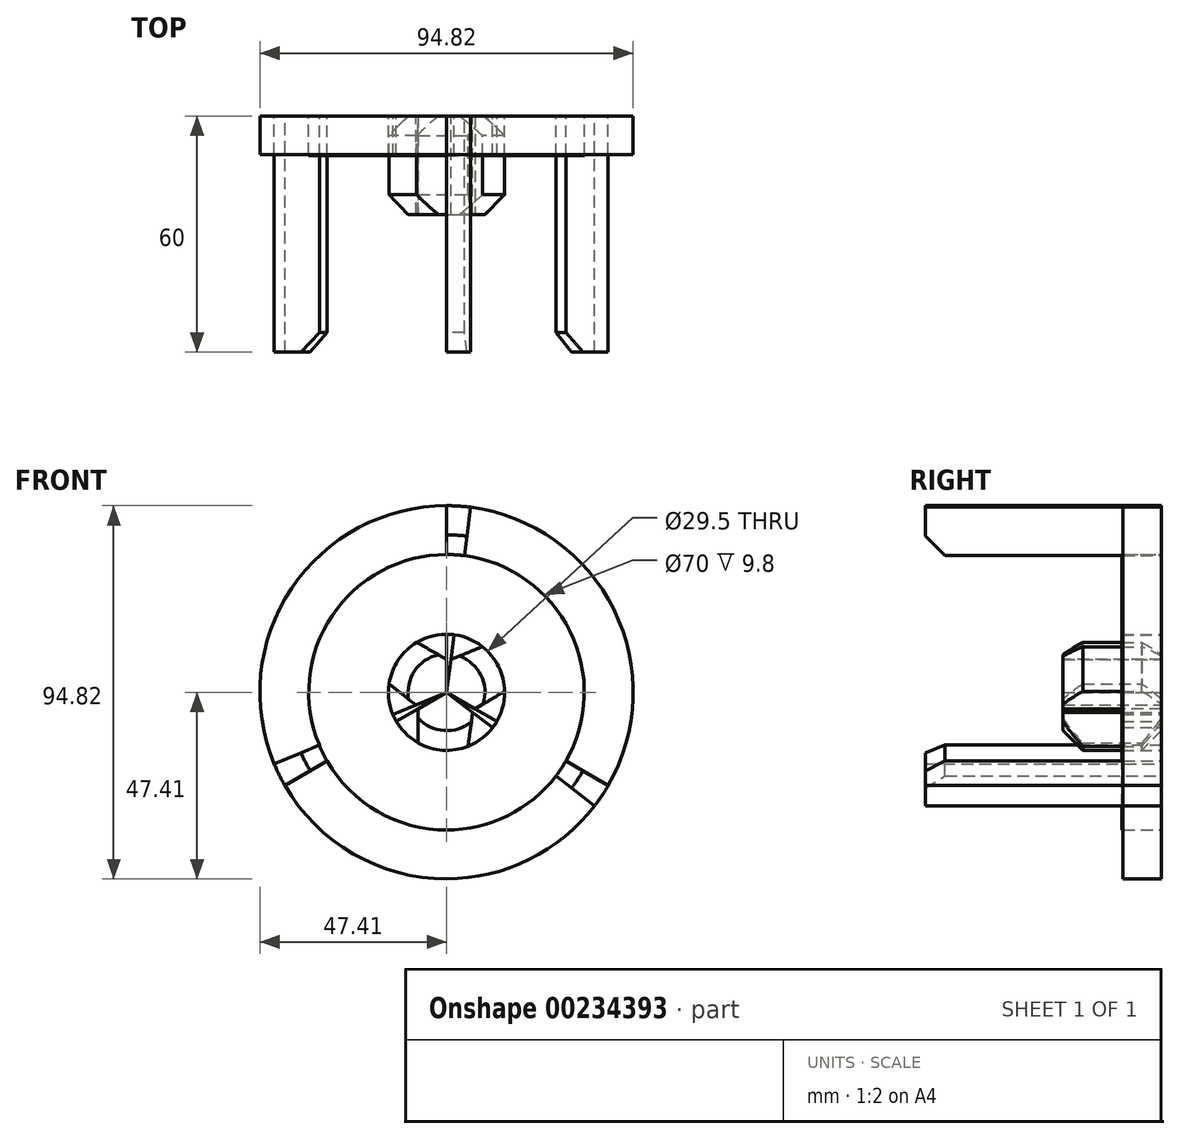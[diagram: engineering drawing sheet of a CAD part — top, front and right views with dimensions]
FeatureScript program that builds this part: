
annotation { "Feature Type Name" : "Feature", "Feature Type Description" : "" }
export const myFeature = defineFeature(function(context is Context, id is Id, definition is map)
    precondition{}
    {
        {
            var Q0;
            Q0=qCreatedBy(makeId("Front.planeOp"),FACE);
            var sketch = newSketch(context, id + "F0", { "sketchPlane" : qUnion([Q0])});
            skCircle(sketch, "E0", {"center": v(0, 0) * mm, "radius": 35 * mm});
            skCircle(sketch, "E1", {"center": v(0, 0) * mm, "radius": 47.41 * mm});
            skLineSegment(sketch, "E2", {"start": v(0, 0) * mm, "end": v(0, 47.41) * mm});
            skLineSegment(sketch, "E3.1.0", {"start": v(0, 0) * mm, "end": v(-41.06, -23.7) * mm});
            skLineSegment(sketch, "E3.2.0", {"start": v(0, 0) * mm, "end": v(41.06, -23.7) * mm});
            skLineSegment(sketch, "E4", {"start": v(0, 0) * mm, "end": v(6.14, 47.01) * mm});
            skLineSegment(sketch, "E5.1.0", {"start": v(0, 0) * mm, "end": v(-43.79, -18.2) * mm});
            skLineSegment(sketch, "E5.2.0", {"start": v(0, 0) * mm, "end": v(37.65, -28.82) * mm});
            skCircle(sketch, "E6", {"center": v(0, 0) * mm, "radius": 14.75 * mm});
            skSolve(sketch);
        }
        {
            var Q0;
            {var subQ0=sQuery(id+"F0.wireOp",EDGE,"E2");var subQ1=sQuery(id+"F0.wireOp",EDGE,"E0");var subQ2=makeQuery(id+"F0.imprint","INTERSECT",VERTEX,{"derivedFrom":[subQ1,subQ0]});Q0=makeQuery(id+"F0.imprint","IMPRINT",FACE,{"disambiguationData":[TD([[makeQuery(id+"F0.imprint","IMPRINT",EDGE,{"disambiguationData":[TD([[subQ2,1.0]])],"derivedFrom":subQ1}),-1.0]])]});}
            var Q1;
            {var subQ0=sQuery(id+"F0.wireOp",EDGE,"E5.2.0");var subQ1=sQuery(id+"F0.wireOp",EDGE,"E0");var subQ2=makeQuery(id+"F0.imprint","INTERSECT",VERTEX,{"derivedFrom":[subQ1,subQ0]});Q1=makeQuery(id+"F0.imprint","IMPRINT",FACE,{"disambiguationData":[TD([[makeQuery(id+"F0.imprint","IMPRINT",EDGE,{"disambiguationData":[TD([[subQ2,-1.0]])],"derivedFrom":subQ1}),-1.0]])]});}
            var Q2;
            {var subQ0=sQuery(id+"F0.wireOp",EDGE,"E5.1.0");var subQ1=sQuery(id+"F0.wireOp",EDGE,"E0");var subQ2=makeQuery(id+"F0.imprint","INTERSECT",VERTEX,{"derivedFrom":[subQ1,subQ0]});Q2=makeQuery(id+"F0.imprint","IMPRINT",FACE,{"disambiguationData":[TD([[makeQuery(id+"F0.imprint","IMPRINT",EDGE,{"disambiguationData":[TD([[subQ2,-1.0]])],"derivedFrom":subQ1}),-1.0]])]});}
            extrude(context, id + "F1", {"entities" : qUnion([Q0, Q1, Q2]), "depth" : 60 * mm});
        }
        {
            var Q0;
            Q0 = qSketchRegion(id + "F0", true);
            extrude(context, id + "F2", {"entities" : qUnion([Q0]), "depth" : 9.8 * mm});
        }
        {
            var Q0;
            {var subQ1=sQuery(id+"F0.wireOp",EDGE,"E2");var subQ3=sQuery(id+"F0.wireOp",EDGE,"E6");var subQ4=makeQuery(id+"F0.imprint","INTERSECT",VERTEX,{"derivedFrom":[subQ1,subQ3]});Q0=makeQuery(id+"F0.imprint","IMPRINT",FACE,{"disambiguationData":[TD([[makeQuery(id+"F0.imprint","IMPRINT",EDGE,{"disambiguationData":[TD([[subQ4,-1.0]])],"derivedFrom":subQ3}),1.0]])]});}
            var Q1;
            {var subQ1=sQuery(id+"F0.wireOp",EDGE,"E3.2.0");var subQ3=sQuery(id+"F0.wireOp",EDGE,"E6");var subQ4=makeQuery(id+"F0.imprint","INTERSECT",VERTEX,{"derivedFrom":[subQ1,subQ3]});Q1=makeQuery(id+"F0.imprint","IMPRINT",FACE,{"disambiguationData":[TD([[makeQuery(id+"F0.imprint","IMPRINT",EDGE,{"disambiguationData":[TD([[subQ4,-1.0]])],"derivedFrom":subQ3}),1.0]])]});}
            var Q2;
            {var subQ1=sQuery(id+"F0.wireOp",EDGE,"E3.1.0");var subQ3=sQuery(id+"F0.wireOp",EDGE,"E6");var subQ4=makeQuery(id+"F0.imprint","INTERSECT",VERTEX,{"derivedFrom":[subQ1,subQ3]});Q2=makeQuery(id+"F0.imprint","IMPRINT",FACE,{"disambiguationData":[TD([[makeQuery(id+"F0.imprint","IMPRINT",EDGE,{"disambiguationData":[TD([[subQ4,-1.0]])],"derivedFrom":subQ3}),1.0]])]});}
            extrude(context, id + "F3", {"entities" : qUnion([Q0, Q1, Q2]), "depth" : 25 * mm});
        }
        {
            var Q0;
            {var subQ0=sQuery(id+"F0.wireOp",EDGE,"E3.1.0");var subQ1=sQuery(id+"F0.wireOp",EDGE,"E0");var subQ2=makeQuery(id+"F0.imprint","INTERSECT",VERTEX,{"derivedFrom":[subQ1,subQ0]});Q0=makeQuery(id+"F0.imprint","IMPRINT",FACE,{"disambiguationData":[TD([[makeQuery(id+"F0.imprint","IMPRINT",EDGE,{"disambiguationData":[TD([[subQ2,-1.0]])],"derivedFrom":subQ1}),1.0]])]});}
            var Q1;
            {var subQ0=sQuery(id+"F0.wireOp",EDGE,"E4");var subQ1=sQuery(id+"F0.wireOp",EDGE,"E0");var subQ2=makeQuery(id+"F0.imprint","INTERSECT",VERTEX,{"derivedFrom":[subQ1,subQ0]});Q1=makeQuery(id+"F0.imprint","IMPRINT",FACE,{"disambiguationData":[TD([[makeQuery(id+"F0.imprint","IMPRINT",EDGE,{"disambiguationData":[TD([[subQ2,1.0]])],"derivedFrom":subQ1}),1.0]])]});}
            var Q2;
            {var subQ0=sQuery(id+"F0.wireOp",EDGE,"E5.2.0");var subQ1=sQuery(id+"F0.wireOp",EDGE,"E0");var subQ2=makeQuery(id+"F0.imprint","INTERSECT",VERTEX,{"derivedFrom":[subQ1,subQ0]});Q2=makeQuery(id+"F0.imprint","IMPRINT",FACE,{"disambiguationData":[TD([[makeQuery(id+"F0.imprint","IMPRINT",EDGE,{"disambiguationData":[TD([[subQ2,-1.0]])],"derivedFrom":subQ1}),1.0]])]});}
            var Q3;
            {var subQ0=sQuery(id+"F0.wireOp",EDGE,"E5.1.0");var subQ1=sQuery(id+"F0.wireOp",EDGE,"E0");var subQ2=makeQuery(id+"F0.imprint","INTERSECT",VERTEX,{"derivedFrom":[subQ1,subQ0]});Q3=makeQuery(id+"F0.imprint","IMPRINT",FACE,{"disambiguationData":[TD([[makeQuery(id+"F0.imprint","IMPRINT",EDGE,{"disambiguationData":[TD([[subQ2,-1.0]])],"derivedFrom":subQ1}),1.0]])]});}
            var Q4;
            {var subQ0=sQuery(id+"F0.wireOp",EDGE,"E2");var subQ1=sQuery(id+"F0.wireOp",EDGE,"E0");var subQ2=makeQuery(id+"F0.imprint","INTERSECT",VERTEX,{"derivedFrom":[subQ1,subQ0]});Q4=makeQuery(id+"F0.imprint","IMPRINT",FACE,{"disambiguationData":[TD([[makeQuery(id+"F0.imprint","IMPRINT",EDGE,{"disambiguationData":[TD([[subQ2,-1.0]])],"derivedFrom":subQ1}),1.0]])]});}
            var Q5;
            {var subQ0=sQuery(id+"F0.wireOp",EDGE,"E2");var subQ1=sQuery(id+"F0.wireOp",EDGE,"E0");var subQ2=makeQuery(id+"F0.imprint","INTERSECT",VERTEX,{"derivedFrom":[subQ1,subQ0]});Q5=makeQuery(id+"F0.imprint","IMPRINT",FACE,{"disambiguationData":[TD([[makeQuery(id+"F0.imprint","IMPRINT",EDGE,{"disambiguationData":[TD([[subQ2,1.0]])],"derivedFrom":subQ1}),1.0]])]});}
            extrude(context, id + "F4", {"entities" : qUnion([Q0, Q1, Q2, Q3, Q4, Q5]), "depth" : 10 * mm});
        }
        {
            var Q0;
            {var subQ1=sQuery(id+"F0.wireOp",EDGE,"E3.2.0");var subQ3=sQuery(id+"F0.wireOp",EDGE,"E6");var subQ4=makeQuery(id+"F0.imprint","INTERSECT",VERTEX,{"derivedFrom":[subQ1,subQ3]});Q0=makeQuery(id+"F0.imprint","IMPRINT",FACE,{"disambiguationData":[TD([[makeQuery(id+"F0.imprint","IMPRINT",EDGE,{"disambiguationData":[TD([[subQ4,1.0]])],"derivedFrom":subQ3}),1.0]])]});}
            var Q1;
            {var subQ1=sQuery(id+"F0.wireOp",EDGE,"E3.1.0");var subQ3=sQuery(id+"F0.wireOp",EDGE,"E6");var subQ4=makeQuery(id+"F0.imprint","INTERSECT",VERTEX,{"derivedFrom":[subQ1,subQ3]});Q1=makeQuery(id+"F0.imprint","IMPRINT",FACE,{"disambiguationData":[TD([[makeQuery(id+"F0.imprint","IMPRINT",EDGE,{"disambiguationData":[TD([[subQ4,1.0]])],"derivedFrom":subQ3}),1.0]])]});}
            var Q2;
            {var subQ1=sQuery(id+"F0.wireOp",EDGE,"E2");var subQ3=sQuery(id+"F0.wireOp",EDGE,"E6");var subQ4=makeQuery(id+"F0.imprint","INTERSECT",VERTEX,{"derivedFrom":[subQ1,subQ3]});Q2=makeQuery(id+"F0.imprint","IMPRINT",FACE,{"disambiguationData":[TD([[makeQuery(id+"F0.imprint","IMPRINT",EDGE,{"disambiguationData":[TD([[subQ4,1.0]])],"derivedFrom":subQ3}),1.0]])]});}
            extrude(context, id + "F5", {"entities" : qUnion([Q0, Q1, Q2]), "depth" : 10 * mm});
        }
        {
            var Q0;
            {var subQ0=sQuery(id+"F0.wireOp",EDGE,"E6");Q0=makeQuery(id+"F3.opExtrude","SWEPT_FACE",FACE,{"disambiguationData":[OSD([subQ0]),TDD([makeQuery(id+"F0.imprint","IMPRINT",EDGE,{"disambiguationData":[TD([[makeQuery(id+"F0.imprint","INTERSECT",VERTEX,{"derivedFrom":[sQuery(id+"F0.wireOp",EDGE,"E3.2.0"),subQ0]}),-1.0]])],"derivedFrom":subQ0})])]});}
            var Q1;
            {var subQ0=sQuery(id+"F0.wireOp",EDGE,"E6");Q1=makeQuery(id+"F3.opExtrude","CAP_EDGE",EDGE,{"disambiguationData":[OSD([subQ0]),TDD([makeQuery(id+"F0.imprint","IMPRINT",EDGE,{"disambiguationData":[TD([[makeQuery(id+"F0.imprint","INTERSECT",VERTEX,{"derivedFrom":[sQuery(id+"F0.wireOp",EDGE,"E3.1.0"),subQ0]}),-1.0]])],"derivedFrom":subQ0})])],"isStart":false});}
            var Q2;
            {var subQ0=sQuery(id+"F0.wireOp",EDGE,"E6");Q2=makeQuery(id+"F3.opExtrude","SWEPT_FACE",FACE,{"disambiguationData":[OSD([subQ0]),TDD([makeQuery(id+"F0.imprint","IMPRINT",EDGE,{"disambiguationData":[TD([[makeQuery(id+"F0.imprint","INTERSECT",VERTEX,{"derivedFrom":[sQuery(id+"F0.wireOp",EDGE,"E3.1.0"),subQ0]}),-1.0]])],"derivedFrom":subQ0})])]});}
            var Q3;
            {var subQ0=sQuery(id+"F0.wireOp",EDGE,"E6");Q3=makeQuery(id+"F3.opExtrude","SWEPT_FACE",FACE,{"disambiguationData":[OSD([subQ0]),TDD([makeQuery(id+"F0.imprint","IMPRINT",EDGE,{"disambiguationData":[TD([[makeQuery(id+"F0.imprint","INTERSECT",VERTEX,{"derivedFrom":[sQuery(id+"F0.wireOp",EDGE,"E2"),subQ0]}),-1.0]])],"derivedFrom":subQ0})])]});}
            chamfer(context, id + "F6", {"entities" : qUnion([Q0, Q1, Q2, Q3]), "width" : 5 * mm, "tangentPropagation" : true});
        }
        {
            var Q0;
            {var subQ0=sQuery(id+"F0.wireOp",EDGE,"E0");Q0=makeQuery(id+"F1.opExtrude","CAP_EDGE",EDGE,{"disambiguationData":[OSD([subQ0]),TDD([makeQuery(id+"F0.imprint","IMPRINT",EDGE,{"disambiguationData":[TD([[makeQuery(id+"F0.imprint","INTERSECT",VERTEX,{"derivedFrom":[subQ0,sQuery(id+"F0.wireOp",EDGE,"E5.1.0")]}),-1.0]])],"derivedFrom":subQ0})])],"isStart":false});}
            var Q1;
            {var subQ0=sQuery(id+"F0.wireOp",EDGE,"E0");Q1=makeQuery(id+"F1.opExtrude","CAP_EDGE",EDGE,{"disambiguationData":[OSD([subQ0]),TDD([makeQuery(id+"F0.imprint","IMPRINT",EDGE,{"disambiguationData":[TD([[makeQuery(id+"F0.imprint","INTERSECT",VERTEX,{"derivedFrom":[subQ0,sQuery(id+"F0.wireOp",EDGE,"E5.2.0")]}),-1.0]])],"derivedFrom":subQ0})])],"isStart":false});}
            var Q2;
            {var subQ0=sQuery(id+"F0.wireOp",EDGE,"E0");Q2=makeQuery(id+"F1.opExtrude","CAP_EDGE",EDGE,{"disambiguationData":[OSD([subQ0]),TDD([makeQuery(id+"F0.imprint","IMPRINT",EDGE,{"disambiguationData":[TD([[makeQuery(id+"F0.imprint","INTERSECT",VERTEX,{"derivedFrom":[subQ0,sQuery(id+"F0.wireOp",EDGE,"E2")]}),1.0]])],"derivedFrom":subQ0})])],"isStart":false});}
            chamfer(context, id + "F7", {"entities" : qUnion([Q0, Q1, Q2]), "width" : 5 * mm, "tangentPropagation" : true});
        }
    });
